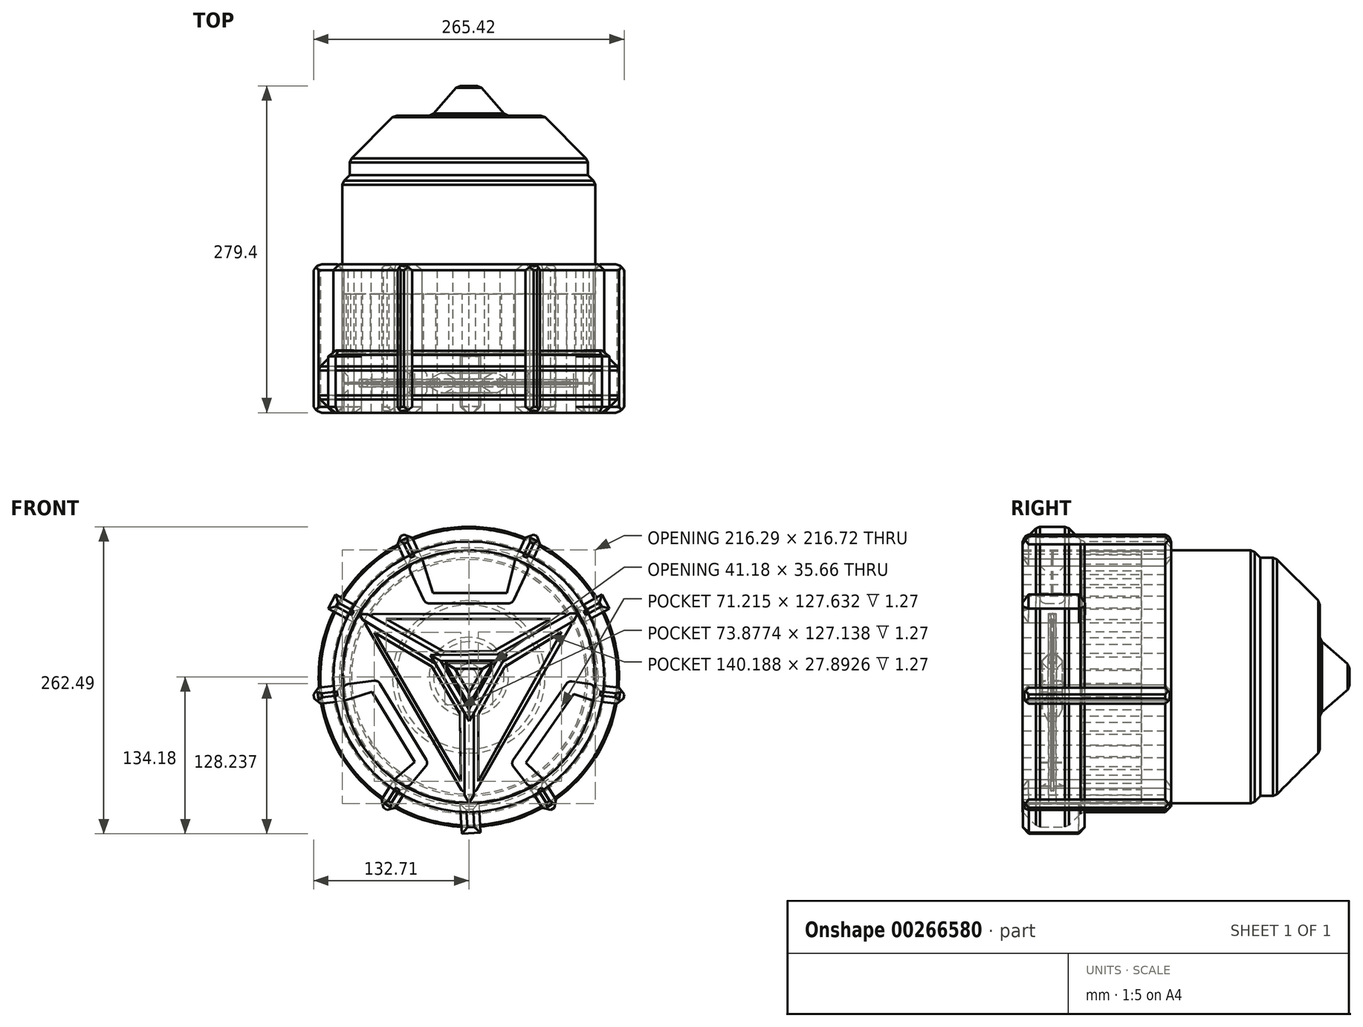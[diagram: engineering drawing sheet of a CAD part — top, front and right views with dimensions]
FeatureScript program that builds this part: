
annotation { "Feature Type Name" : "Feature", "Feature Type Description" : "" }
export const myFeature = defineFeature(function(context is Context, id is Id, definition is map)
    precondition{}
    {
        {
            var Q0;
            Q0=qCreatedBy(makeId("Front.planeOp"),FACE);
            var sketch = newSketch(context, id + "F0", { "sketchPlane" : qUnion([Q0])});
            skLineSegment(sketch, "E0.0", {"start": v(93.23, 54.18) * mm, "end": v(0.3, -107.83) * mm});
            skLineSegment(sketch, "E0.1", {"start": v(0.3, -107.83) * mm, "end": v(-93.54, 53.65) * mm});
            skLineSegment(sketch, "E0.2", {"start": v(-93.54, 53.65) * mm, "end": v(93.23, 54.18) * mm});
            skLineSegment(sketch, "E1.0", {"start": v(-32.94, 18.6) * mm, "end": v(32.57, 19.23) * mm});
            skLineSegment(sketch, "E1.1", {"start": v(32.57, 19.23) * mm, "end": v(0.36, -37.82) * mm});
            skLineSegment(sketch, "E1.2", {"start": v(0.36, -37.82) * mm, "end": v(-32.94, 18.6) * mm});
            skLineSegment(sketch, "E2", {"start": v(4.24, -30.96) * mm, "end": v(4.24, -100.97) * mm});
            skLineSegment(sketch, "E3", {"start": v(-3.69, -100.97) * mm, "end": v(-3.69, -30.96) * mm});
            skLineSegment(sketch, "E4", {"start": v(-86.27, 41.16) * mm, "end": v(-83.71, 36.75) * mm});
            skLineSegment(sketch, "E5", {"start": v(-86.58, 53.67) * mm, "end": v(-24.77, 18.68) * mm});
            skLineSegment(sketch, "E6", {"start": v(-28.9, 11.74) * mm, "end": v(-90.75, 48.87) * mm});
            skLineSegment(sketch, "E7", {"start": v(24.66, 19.15) * mm, "end": v(86.53, 54.16) * mm});
            skLineSegment(sketch, "E8", {"start": v(29.05, 12.98) * mm, "end": v(89.61, 47.87) * mm});
            skCircle(sketch, "E9.cCircle", {"center": v(0, 0) * mm, "radius": 108.36 * mm, "construction": true});
            skLineSegment(sketch, "E9.0", {"start": v(-13.58, -107.5) * mm, "end": v(0, -108.36) * mm});
            skLineSegment(sketch, "E9.1", {"start": v(-26.95, -104.96) * mm, "end": v(-13.58, -107.5) * mm});
            skLineSegment(sketch, "E9.2", {"start": v(-39.9, -100.75) * mm, "end": v(-26.95, -104.96) * mm});
            skLineSegment(sketch, "E9.3", {"start": v(-52.2, -94.96) * mm, "end": v(-39.9, -100.75) * mm});
            skLineSegment(sketch, "E9.4", {"start": v(-63.7, -87.67) * mm, "end": v(-52.2, -94.96) * mm});
            skLineSegment(sketch, "E9.5", {"start": v(-74.18, -79) * mm, "end": v(-63.7, -87.67) * mm});
            skLineSegment(sketch, "E9.6", {"start": v(-83.5, -69.07) * mm, "end": v(-74.18, -79) * mm});
            skLineSegment(sketch, "E9.7", {"start": v(-91.5, -58.06) * mm, "end": v(-83.5, -69.07) * mm});
            skLineSegment(sketch, "E9.8", {"start": v(-98.05, -46.14) * mm, "end": v(-91.5, -58.06) * mm});
            skLineSegment(sketch, "E9.9", {"start": v(-103.06, -33.49) * mm, "end": v(-98.05, -46.14) * mm});
            skLineSegment(sketch, "E9.10", {"start": v(-106.44, -20.3) * mm, "end": v(-103.06, -33.49) * mm});
            skLineSegment(sketch, "E9.11", {"start": v(-108.15, -6.8) * mm, "end": v(-106.44, -20.3) * mm});
            skLineSegment(sketch, "E9.12", {"start": v(-108.15, 6.8) * mm, "end": v(-108.15, -6.8) * mm});
            skLineSegment(sketch, "E9.13", {"start": v(-106.44, 20.3) * mm, "end": v(-108.15, 6.8) * mm});
            skLineSegment(sketch, "E9.14", {"start": v(-103.06, 33.49) * mm, "end": v(-106.44, 20.3) * mm});
            skLineSegment(sketch, "E9.15", {"start": v(-98.05, 46.14) * mm, "end": v(-103.06, 33.49) * mm});
            skLineSegment(sketch, "E9.16", {"start": v(-91.5, 58.06) * mm, "end": v(-98.05, 46.14) * mm});
            skLineSegment(sketch, "E9.17", {"start": v(-83.5, 69.07) * mm, "end": v(-91.5, 58.06) * mm});
            skLineSegment(sketch, "E9.18", {"start": v(-74.18, 79) * mm, "end": v(-83.5, 69.07) * mm});
            skLineSegment(sketch, "E9.19", {"start": v(-63.7, 87.67) * mm, "end": v(-74.18, 79) * mm});
            skLineSegment(sketch, "E9.20", {"start": v(-52.2, 94.96) * mm, "end": v(-63.7, 87.67) * mm});
            skLineSegment(sketch, "E9.21", {"start": v(-39.9, 100.75) * mm, "end": v(-52.2, 94.96) * mm});
            skLineSegment(sketch, "E9.22", {"start": v(-26.95, 104.96) * mm, "end": v(-39.9, 100.75) * mm});
            skLineSegment(sketch, "E9.23", {"start": v(-13.58, 107.5) * mm, "end": v(-26.95, 104.96) * mm});
            skLineSegment(sketch, "E9.24", {"start": v(0, 108.36) * mm, "end": v(-13.58, 107.5) * mm});
            skLineSegment(sketch, "E9.25", {"start": v(13.58, 107.5) * mm, "end": v(0, 108.36) * mm});
            skLineSegment(sketch, "E9.26", {"start": v(26.95, 104.96) * mm, "end": v(13.58, 107.5) * mm});
            skLineSegment(sketch, "E9.27", {"start": v(39.9, 100.75) * mm, "end": v(26.95, 104.96) * mm});
            skLineSegment(sketch, "E9.28", {"start": v(52.2, 94.96) * mm, "end": v(39.9, 100.75) * mm});
            skLineSegment(sketch, "E9.29", {"start": v(63.7, 87.67) * mm, "end": v(52.2, 94.96) * mm});
            skLineSegment(sketch, "E9.30", {"start": v(74.18, 79) * mm, "end": v(63.7, 87.67) * mm});
            skLineSegment(sketch, "E9.31", {"start": v(83.5, 69.07) * mm, "end": v(74.18, 79) * mm});
            skLineSegment(sketch, "E9.32", {"start": v(91.5, 58.06) * mm, "end": v(83.5, 69.07) * mm});
            skLineSegment(sketch, "E9.33", {"start": v(98.05, 46.14) * mm, "end": v(91.5, 58.06) * mm});
            skLineSegment(sketch, "E9.34", {"start": v(103.06, 33.49) * mm, "end": v(98.05, 46.14) * mm});
            skLineSegment(sketch, "E9.35", {"start": v(106.44, 20.3) * mm, "end": v(103.06, 33.49) * mm});
            skLineSegment(sketch, "E9.36", {"start": v(108.15, 6.8) * mm, "end": v(106.44, 20.3) * mm});
            skLineSegment(sketch, "E9.37", {"start": v(108.15, -6.8) * mm, "end": v(108.15, 6.8) * mm});
            skLineSegment(sketch, "E9.38", {"start": v(106.44, -20.3) * mm, "end": v(108.15, -6.8) * mm});
            skLineSegment(sketch, "E9.39", {"start": v(103.06, -33.49) * mm, "end": v(106.44, -20.3) * mm});
            skLineSegment(sketch, "E9.40", {"start": v(98.05, -46.14) * mm, "end": v(103.06, -33.49) * mm});
            skLineSegment(sketch, "E9.41", {"start": v(91.5, -58.06) * mm, "end": v(98.05, -46.14) * mm});
            skLineSegment(sketch, "E9.42", {"start": v(83.5, -69.07) * mm, "end": v(91.5, -58.06) * mm});
            skLineSegment(sketch, "E9.43", {"start": v(74.18, -79) * mm, "end": v(83.5, -69.07) * mm});
            skLineSegment(sketch, "E9.44", {"start": v(63.7, -87.67) * mm, "end": v(74.18, -79) * mm});
            skLineSegment(sketch, "E9.45", {"start": v(52.2, -94.96) * mm, "end": v(63.7, -87.67) * mm});
            skLineSegment(sketch, "E9.46", {"start": v(39.9, -100.75) * mm, "end": v(52.2, -94.96) * mm});
            skLineSegment(sketch, "E9.47", {"start": v(26.95, -104.96) * mm, "end": v(39.9, -100.75) * mm});
            skLineSegment(sketch, "E9.48", {"start": v(13.58, -107.5) * mm, "end": v(26.95, -104.96) * mm});
            skLineSegment(sketch, "E9.49", {"start": v(0, -108.36) * mm, "end": v(13.58, -107.5) * mm});
            skLineSegment(sketch, "E10.0", {"start": v(0, -13.61) * mm, "end": v(-11.79, 6.8) * mm});
            skLineSegment(sketch, "E10.1", {"start": v(-11.79, 6.8) * mm, "end": v(11.79, 6.8) * mm});
            skLineSegment(sketch, "E10.2", {"start": v(11.79, 6.8) * mm, "end": v(0, -13.61) * mm});
            skLineSegment(sketch, "E11", {"start": v(89.74, -14.56) * mm, "end": v(48.6, -73.49) * mm});
            skLineSegment(sketch, "E12", {"start": v(85.15, -3.4) * mm, "end": v(35.89, -73.94) * mm});
            skLineSegment(sketch, "E13", {"start": v(-77.64, -2.95) * mm, "end": v(-34.5, -73.94) * mm});
            skLineSegment(sketch, "E14", {"start": v(-82.82, -12.87) * mm, "end": v(-46.16, -72.86) * mm});
            skLineSegment(sketch, "E15", {"start": v(-37.12, 62.9) * mm, "end": v(37.12, 62.9) * mm});
            skLineSegment(sketch, "E16", {"start": v(-30.7, 71.54) * mm, "end": v(32.57, 71.54) * mm});
            skLineSegment(sketch, "E17", {"start": v(35.89, -73.94) * mm, "end": v(52.2, -94.96) * mm});
            skLineSegment(sketch, "E18", {"start": v(48.6, -73.49) * mm, "end": v(63.7, -87.67) * mm});
            skLineSegment(sketch, "E19", {"start": v(85.15, -3.4) * mm, "end": v(108.15, -6.8) * mm});
            skLineSegment(sketch, "E20", {"start": v(89.74, -14.56) * mm, "end": v(106.44, -20.3) * mm});
            skLineSegment(sketch, "E21", {"start": v(-82.82, -12.87) * mm, "end": v(-106.44, -20.3) * mm});
            skLineSegment(sketch, "E22", {"start": v(-77.64, -2.95) * mm, "end": v(-108.15, -6.8) * mm});
            skLineSegment(sketch, "E23", {"start": v(-46.16, -72.86) * mm, "end": v(-63.7, -87.67) * mm});
            skLineSegment(sketch, "E24", {"start": v(-34.5, -73.94) * mm, "end": v(-52.2, -94.96) * mm});
            skLineSegment(sketch, "E25", {"start": v(-30.7, 71.54) * mm, "end": v(-39.9, 100.75) * mm});
            skLineSegment(sketch, "E26", {"start": v(32.57, 71.54) * mm, "end": v(39.9, 100.75) * mm});
            skLineSegment(sketch, "E27", {"start": v(37.12, 62.9) * mm, "end": v(52.2, 94.96) * mm});
            skLineSegment(sketch, "E28", {"start": v(-37.12, 62.9) * mm, "end": v(-52.2, 94.96) * mm});
            skCircle(sketch, "E29.0", {"center": v(0, 0) * mm, "radius": 128.3 * mm});
            skSolve(sketch);
        }
        {
            var Q0;
            Q0=makeQuery(id+"F0.imprint","IMPRINT",FACE,{"disambiguationData":[TD([[makeQuery(id+"F0.imprint","IMPRINT",EDGE,{"derivedFrom":sQuery(id+"F0.wireOp",EDGE,"E9.0")}),-1.0]])]});
            extrude(context, id + "F1", {"entities" : qUnion([Q0]), "endBound" : BoundingType.SYMMETRIC, "depth" : 50.8 * mm});
        }
        {
            var Q0;
            {var subQ0=sQuery(id+"F0.wireOp",EDGE,"E5");Q0=makeQuery(id+"F0.imprint","IMPRINT",FACE,{"disambiguationData":[TD([[makeQuery(id+"F0.imprint","IMPRINT",EDGE,{"derivedFrom":subQ0}),1.0]])]});}
            var Q1;
            {var subQ0=sQuery(id+"F0.wireOp",EDGE,"E3");Q1=makeQuery(id+"F0.imprint","IMPRINT",FACE,{"disambiguationData":[TD([[makeQuery(id+"F0.imprint","IMPRINT",EDGE,{"derivedFrom":subQ0}),1.0]])]});}
            var Q2;
            {var subQ0=sQuery(id+"F0.wireOp",EDGE,"E2");Q2=makeQuery(id+"F0.imprint","IMPRINT",FACE,{"disambiguationData":[TD([[makeQuery(id+"F0.imprint","IMPRINT",EDGE,{"derivedFrom":subQ0}),1.0]])]});}
            extrude(context, id + "F2", {"entities" : qUnion([Q0, Q1, Q2]), "endBound" : BoundingType.SYMMETRIC, "depth" : 2.54 * mm});
        }
        {
            var Q0;
            {var subQ7=sQuery(id+"F0.wireOp",EDGE,"E5");Q0=makeQuery(id+"F0.imprint","IMPRINT",FACE,{"disambiguationData":[TD([[makeQuery(id+"F0.imprint","IMPRINT",EDGE,{"derivedFrom":subQ7}),-1.0]])]});}
            var Q1;
            {var subQ4=sQuery(id+"F0.wireOp",EDGE,"E7");Q1=makeQuery(id+"F0.imprint","IMPRINT",FACE,{"disambiguationData":[TD([[makeQuery(id+"F0.imprint","IMPRINT",EDGE,{"derivedFrom":subQ4}),-1.0]])]});}
            var Q2;
            {var subQ3=sQuery(id+"F0.wireOp",EDGE,"E2");Q2=makeQuery(id+"F0.imprint","IMPRINT",FACE,{"disambiguationData":[TD([[makeQuery(id+"F0.imprint","IMPRINT",EDGE,{"derivedFrom":subQ3}),-1.0]])]});}
            extrude(context, id + "F3", {"entities" : qUnion([Q0, Q1, Q2]), "endBound" : BoundingType.SYMMETRIC, "depth" : 6.35 * mm});
        }
        {
            var Q0;
            Q0=makeQuery(id+"F0.imprint","IMPRINT",FACE,{"disambiguationData":[TD([[makeQuery(id+"F0.imprint","IMPRINT",EDGE,{"derivedFrom":sQuery(id+"F0.wireOp",EDGE,"E10.0")}),-1.0]])]});
            var Q1;
            {var subQ0=sQuery(id+"F0.wireOp",EDGE,"E4");Q1=makeQuery(id+"F0.imprint","IMPRINT",FACE,{"disambiguationData":[TD([[makeQuery(id+"F0.imprint","IMPRINT",EDGE,{"derivedFrom":subQ0}),-1.0]])]});}
            var Q2;
            Q2=makeQuery(id+"F0.imprint","IMPRINT",FACE,{"disambiguationData":[TD([[makeQuery(id+"F0.imprint","IMPRINT",EDGE,{"derivedFrom":sQuery(id+"F0.wireOp",EDGE,"E9.22")}),1.0]])]});
            var Q3;
            Q3=makeQuery(id+"F0.imprint","IMPRINT",FACE,{"disambiguationData":[TD([[makeQuery(id+"F0.imprint","IMPRINT",EDGE,{"derivedFrom":sQuery(id+"F0.wireOp",EDGE,"E9.39")}),1.0]])]});
            var Q4;
            Q4=makeQuery(id+"F0.imprint","IMPRINT",FACE,{"disambiguationData":[TD([[makeQuery(id+"F0.imprint","IMPRINT",EDGE,{"derivedFrom":sQuery(id+"F0.wireOp",EDGE,"E9.5")}),1.0]])]});
            extrude(context, id + "F4", {"entities" : qUnion([Q0, Q1, Q2, Q3, Q4]), "endBound" : BoundingType.SYMMETRIC, "depth" : 1.27 * mm});
        }
        {
            var Q0;
            Q0=makeQuery(id+"F0.imprint","IMPRINT",FACE,{"disambiguationData":[TD([[makeQuery(id+"F0.imprint","IMPRINT",EDGE,{"derivedFrom":sQuery(id+"F0.wireOp",EDGE,"E9.21")}),1.0]])]});
            var Q1;
            Q1=makeQuery(id+"F0.imprint","IMPRINT",FACE,{"disambiguationData":[TD([[makeQuery(id+"F0.imprint","IMPRINT",EDGE,{"derivedFrom":sQuery(id+"F0.wireOp",EDGE,"E9.4")}),1.0]])]});
            var Q2;
            Q2=makeQuery(id+"F0.imprint","IMPRINT",FACE,{"disambiguationData":[TD([[makeQuery(id+"F0.imprint","IMPRINT",EDGE,{"derivedFrom":sQuery(id+"F0.wireOp",EDGE,"E9.38")}),1.0]])]});
            extrude(context, id + "F5", {"entities" : qUnion([Q0, Q1, Q2]), "endBound" : BoundingType.SYMMETRIC, "depth" : 21.59 * mm});
        }
        {
            var Q0;
            Q0=makeQuery(id+"F0.imprint","IMPRINT",FACE,{"disambiguationData":[TD([[makeQuery(id+"F0.imprint","IMPRINT",EDGE,{"derivedFrom":sQuery(id+"F0.wireOp",EDGE,"E10.0")}),1.0]])]});
            extrude(context, id + "F6", {"entities" : qUnion([Q0]), "endBound" : BoundingType.SYMMETRIC, "depth" : 17.02 * mm});
        }
        {
            var Q0;
            Q0=makeQuery(id+"F1.opExtrude","CAP_EDGE",EDGE,{"disambiguationData":[OSD([sQuery(id+"F0.wireOp",EDGE,"E29.0")])],"isStart":false});
            var Q1;
            Q1=makeQuery(id+"F1.opExtrude","CAP_EDGE",EDGE,{"disambiguationData":[OSD([sQuery(id+"F0.wireOp",EDGE,"E29.0")])],"isStart":true});
            chamfer(context, id + "F7", {"entities" : qUnion([Q0, Q1]), "width" : 12.7 * mm, "tangentPropagation" : true});
        }
        {
            var Q0;
            Q0=makeQuery(id+"F5.opExtrude","SWEPT_FACE",FACE,{"disambiguationData":[OSD([sQuery(id+"F0.wireOp",EDGE,"E15")])]});
            var Q1;
            Q1=makeQuery(id+"F5.opExtrude","SWEPT_FACE",FACE,{"disambiguationData":[OSD([sQuery(id+"F0.wireOp",EDGE,"E28")])]});
            var Q2;
            Q2=makeQuery(id+"F5.opExtrude","SWEPT_FACE",FACE,{"disambiguationData":[OSD([sQuery(id+"F0.wireOp",EDGE,"E27")])]});
            var Q3;
            Q3=makeQuery(id+"F5.opExtrude","SWEPT_FACE",FACE,{"disambiguationData":[OSD([sQuery(id+"F0.wireOp",EDGE,"E13")])]});
            var Q4;
            Q4=makeQuery(id+"F5.opExtrude","SWEPT_FACE",FACE,{"disambiguationData":[OSD([sQuery(id+"F0.wireOp",EDGE,"E24")])]});
            var Q5;
            Q5=makeQuery(id+"F5.opExtrude","SWEPT_FACE",FACE,{"disambiguationData":[OSD([sQuery(id+"F0.wireOp",EDGE,"E22")])]});
            var Q6;
            Q6=makeQuery(id+"F5.opExtrude","SWEPT_FACE",FACE,{"disambiguationData":[OSD([sQuery(id+"F0.wireOp",EDGE,"E12")])]});
            var Q7;
            Q7=makeQuery(id+"F5.opExtrude","SWEPT_FACE",FACE,{"disambiguationData":[OSD([sQuery(id+"F0.wireOp",EDGE,"E19")])]});
            var Q8;
            Q8=makeQuery(id+"F5.opExtrude","SWEPT_FACE",FACE,{"disambiguationData":[OSD([sQuery(id+"F0.wireOp",EDGE,"E17")])]});
            fillet(context, id + "F8", {"entities" : qUnion([Q0, Q1, Q2, Q3, Q4, Q5, Q6, Q7, Q8]), "radius" : 5.08 * mm, "tangentPropagation" : true, "allowEdgeOverflow" : false});
        }
        {
            var Q0;
            Q0=makeQuery(id+"F2.opExtrude","SWEPT_FACE",FACE,{"disambiguationData":[OSD([sQuery(id+"F0.wireOp",EDGE,"E0.0")])]});
            var Q1;
            Q1=makeQuery(id+"F2.opExtrude","SWEPT_FACE",FACE,{"disambiguationData":[OSD([sQuery(id+"F0.wireOp",EDGE,"E0.2")])]});
            var Q2;
            Q2=makeQuery(id+"F2.opExtrude","SWEPT_FACE",FACE,{"disambiguationData":[OSD([sQuery(id+"F0.wireOp",EDGE,"E0.1"),sQuery(id+"F0.wireOp",EDGE,"E4")])]});
            fillet(context, id + "F9", {"entities" : qUnion([Q0, Q1, Q2]), "radius" : 1.27 * mm, "tangentPropagation" : true, "allowEdgeOverflow" : false});
        }
        {
            var Q0;
            Q0=makeQuery(id+"F6.opExtrude","CAP_FACE",FACE,{"disambiguationData":[OSD([sQuery(id+"F0.wireOp",EDGE,"E1.0"),sQuery(id+"F0.wireOp",EDGE,"E1.1"),sQuery(id+"F0.wireOp",EDGE,"E1.2"),sQuery(id+"F0.wireOp",EDGE,"E10.0"),sQuery(id+"F0.wireOp",EDGE,"E10.1"),sQuery(id+"F0.wireOp",EDGE,"E10.2")])],"isStart":false});
            var Q1;
            Q1=makeQuery(id+"F6.opExtrude","CAP_FACE",FACE,{"disambiguationData":[OSD([sQuery(id+"F0.wireOp",EDGE,"E1.0"),sQuery(id+"F0.wireOp",EDGE,"E1.1"),sQuery(id+"F0.wireOp",EDGE,"E1.2"),sQuery(id+"F0.wireOp",EDGE,"E10.0"),sQuery(id+"F0.wireOp",EDGE,"E10.1"),sQuery(id+"F0.wireOp",EDGE,"E10.2")])],"isStart":true});
            chamfer(context, id + "F10", {"entities" : qUnion([Q0, Q1]), "width" : 5.08 * mm, "tangentPropagation" : true});
        }
        {
            var Q0;
            Q0=makeQuery(id+"F1.opExtrude","CAP_FACE",FACE,{"disambiguationData":[OSD([sQuery(id+"F0.wireOp",EDGE,"E9.0"),sQuery(id+"F0.wireOp",EDGE,"E9.1"),sQuery(id+"F0.wireOp",EDGE,"E9.2"),sQuery(id+"F0.wireOp",EDGE,"E9.3"),sQuery(id+"F0.wireOp",EDGE,"E9.4"),sQuery(id+"F0.wireOp",EDGE,"E9.5"),sQuery(id+"F0.wireOp",EDGE,"E9.6"),sQuery(id+"F0.wireOp",EDGE,"E9.7"),sQuery(id+"F0.wireOp",EDGE,"E9.8"),sQuery(id+"F0.wireOp",EDGE,"E9.9"),sQuery(id+"F0.wireOp",EDGE,"E9.10"),sQuery(id+"F0.wireOp",EDGE,"E9.11"),sQuery(id+"F0.wireOp",EDGE,"E9.12"),sQuery(id+"F0.wireOp",EDGE,"E9.13"),sQuery(id+"F0.wireOp",EDGE,"E9.14"),sQuery(id+"F0.wireOp",EDGE,"E9.15"),sQuery(id+"F0.wireOp",EDGE,"E9.16"),sQuery(id+"F0.wireOp",EDGE,"E9.17"),sQuery(id+"F0.wireOp",EDGE,"E9.18"),sQuery(id+"F0.wireOp",EDGE,"E9.19"),sQuery(id+"F0.wireOp",EDGE,"E9.20"),sQuery(id+"F0.wireOp",EDGE,"E9.21"),sQuery(id+"F0.wireOp",EDGE,"E9.22"),sQuery(id+"F0.wireOp",EDGE,"E9.23"),sQuery(id+"F0.wireOp",EDGE,"E9.24"),sQuery(id+"F0.wireOp",EDGE,"E9.25"),sQuery(id+"F0.wireOp",EDGE,"E9.26"),sQuery(id+"F0.wireOp",EDGE,"E9.27"),sQuery(id+"F0.wireOp",EDGE,"E9.28"),sQuery(id+"F0.wireOp",EDGE,"E9.29"),sQuery(id+"F0.wireOp",EDGE,"E9.30"),sQuery(id+"F0.wireOp",EDGE,"E9.31"),sQuery(id+"F0.wireOp",EDGE,"E9.32"),sQuery(id+"F0.wireOp",EDGE,"E9.33"),sQuery(id+"F0.wireOp",EDGE,"E9.34"),sQuery(id+"F0.wireOp",EDGE,"E9.35"),sQuery(id+"F0.wireOp",EDGE,"E9.36"),sQuery(id+"F0.wireOp",EDGE,"E9.37"),sQuery(id+"F0.wireOp",EDGE,"E9.38"),sQuery(id+"F0.wireOp",EDGE,"E9.39"),sQuery(id+"F0.wireOp",EDGE,"E9.40"),sQuery(id+"F0.wireOp",EDGE,"E9.41"),sQuery(id+"F0.wireOp",EDGE,"E9.42"),sQuery(id+"F0.wireOp",EDGE,"E9.43"),sQuery(id+"F0.wireOp",EDGE,"E9.44"),sQuery(id+"F0.wireOp",EDGE,"E9.45"),sQuery(id+"F0.wireOp",EDGE,"E9.46"),sQuery(id+"F0.wireOp",EDGE,"E9.47"),sQuery(id+"F0.wireOp",EDGE,"E9.48"),sQuery(id+"F0.wireOp",EDGE,"E9.49"),sQuery(id+"F0.wireOp",EDGE,"E29.0")])],"isStart":true});
            extrude(context, id + "F11", {"entities" : qUnion([Q0]), "operationType" : NewBodyOperationType.ADD, "depth" : 76.2 * mm});
        }
        {
            var Q0;
            Q0=makeQuery(id+"F11.opExtrude","CAP_FACE",FACE,{"disambiguationData":[OSD([sQuery(id+"F0.wireOp",EDGE,"E9.0"),sQuery(id+"F0.wireOp",EDGE,"E9.1"),sQuery(id+"F0.wireOp",EDGE,"E9.2"),sQuery(id+"F0.wireOp",EDGE,"E9.3"),sQuery(id+"F0.wireOp",EDGE,"E9.4"),sQuery(id+"F0.wireOp",EDGE,"E9.5"),sQuery(id+"F0.wireOp",EDGE,"E9.6"),sQuery(id+"F0.wireOp",EDGE,"E9.7"),sQuery(id+"F0.wireOp",EDGE,"E9.8"),sQuery(id+"F0.wireOp",EDGE,"E9.9"),sQuery(id+"F0.wireOp",EDGE,"E9.10"),sQuery(id+"F0.wireOp",EDGE,"E9.11"),sQuery(id+"F0.wireOp",EDGE,"E9.12"),sQuery(id+"F0.wireOp",EDGE,"E9.13"),sQuery(id+"F0.wireOp",EDGE,"E9.14"),sQuery(id+"F0.wireOp",EDGE,"E9.15"),sQuery(id+"F0.wireOp",EDGE,"E9.16"),sQuery(id+"F0.wireOp",EDGE,"E9.17"),sQuery(id+"F0.wireOp",EDGE,"E9.18"),sQuery(id+"F0.wireOp",EDGE,"E9.19"),sQuery(id+"F0.wireOp",EDGE,"E9.20"),sQuery(id+"F0.wireOp",EDGE,"E9.21"),sQuery(id+"F0.wireOp",EDGE,"E9.22"),sQuery(id+"F0.wireOp",EDGE,"E9.23"),sQuery(id+"F0.wireOp",EDGE,"E9.24"),sQuery(id+"F0.wireOp",EDGE,"E9.25"),sQuery(id+"F0.wireOp",EDGE,"E9.26"),sQuery(id+"F0.wireOp",EDGE,"E9.27"),sQuery(id+"F0.wireOp",EDGE,"E9.28"),sQuery(id+"F0.wireOp",EDGE,"E9.29"),sQuery(id+"F0.wireOp",EDGE,"E9.30"),sQuery(id+"F0.wireOp",EDGE,"E9.31"),sQuery(id+"F0.wireOp",EDGE,"E9.32"),sQuery(id+"F0.wireOp",EDGE,"E9.33"),sQuery(id+"F0.wireOp",EDGE,"E9.34"),sQuery(id+"F0.wireOp",EDGE,"E9.35"),sQuery(id+"F0.wireOp",EDGE,"E9.36"),sQuery(id+"F0.wireOp",EDGE,"E9.37"),sQuery(id+"F0.wireOp",EDGE,"E9.38"),sQuery(id+"F0.wireOp",EDGE,"E9.39"),sQuery(id+"F0.wireOp",EDGE,"E9.40"),sQuery(id+"F0.wireOp",EDGE,"E9.41"),sQuery(id+"F0.wireOp",EDGE,"E9.42"),sQuery(id+"F0.wireOp",EDGE,"E9.43"),sQuery(id+"F0.wireOp",EDGE,"E9.44"),sQuery(id+"F0.wireOp",EDGE,"E9.45"),sQuery(id+"F0.wireOp",EDGE,"E9.46"),sQuery(id+"F0.wireOp",EDGE,"E9.47"),sQuery(id+"F0.wireOp",EDGE,"E9.48"),sQuery(id+"F0.wireOp",EDGE,"E9.49"),sQuery(id+"F0.wireOp",EDGE,"E29.0")])],"isStart":false});
            var sketch = newSketch(context, id + "F12", { "sketchPlane" : qUnion([Q0])});
            skCircle(sketch, "E30", {"center": v(0, 0) * mm, "radius": 108.15 * mm});
            skSolve(sketch);
        }
        {
            var Q0;
            Q0=qSketchRegion(id+"F12",true);
            extrude(context, id + "F13", {"entities" : qUnion([Q0]), "depth" : 50.8 * mm});
        }
        {
            var Q0;
            Q0=makeQuery(id+"F11.opExtrude","SWEPT_FACE",FACE,{"disambiguationData":[OSD([sQuery(id+"F0.wireOp",EDGE,"E9.0"),sQuery(id+"F0.wireOp",EDGE,"E9.1"),sQuery(id+"F0.wireOp",EDGE,"E9.2"),sQuery(id+"F0.wireOp",EDGE,"E9.3"),sQuery(id+"F0.wireOp",EDGE,"E9.4"),sQuery(id+"F0.wireOp",EDGE,"E9.5"),sQuery(id+"F0.wireOp",EDGE,"E9.6"),sQuery(id+"F0.wireOp",EDGE,"E9.7"),sQuery(id+"F0.wireOp",EDGE,"E9.8"),sQuery(id+"F0.wireOp",EDGE,"E9.9"),sQuery(id+"F0.wireOp",EDGE,"E9.10"),sQuery(id+"F0.wireOp",EDGE,"E9.11"),sQuery(id+"F0.wireOp",EDGE,"E9.12"),sQuery(id+"F0.wireOp",EDGE,"E9.13"),sQuery(id+"F0.wireOp",EDGE,"E9.14"),sQuery(id+"F0.wireOp",EDGE,"E9.15"),sQuery(id+"F0.wireOp",EDGE,"E9.16"),sQuery(id+"F0.wireOp",EDGE,"E9.17"),sQuery(id+"F0.wireOp",EDGE,"E9.18"),sQuery(id+"F0.wireOp",EDGE,"E9.19"),sQuery(id+"F0.wireOp",EDGE,"E9.20"),sQuery(id+"F0.wireOp",EDGE,"E9.21"),sQuery(id+"F0.wireOp",EDGE,"E9.22"),sQuery(id+"F0.wireOp",EDGE,"E9.23"),sQuery(id+"F0.wireOp",EDGE,"E9.24"),sQuery(id+"F0.wireOp",EDGE,"E9.25"),sQuery(id+"F0.wireOp",EDGE,"E9.26"),sQuery(id+"F0.wireOp",EDGE,"E9.27"),sQuery(id+"F0.wireOp",EDGE,"E9.28"),sQuery(id+"F0.wireOp",EDGE,"E9.29"),sQuery(id+"F0.wireOp",EDGE,"E9.30"),sQuery(id+"F0.wireOp",EDGE,"E9.31"),sQuery(id+"F0.wireOp",EDGE,"E9.32"),sQuery(id+"F0.wireOp",EDGE,"E9.33"),sQuery(id+"F0.wireOp",EDGE,"E9.34"),sQuery(id+"F0.wireOp",EDGE,"E9.35"),sQuery(id+"F0.wireOp",EDGE,"E9.36"),sQuery(id+"F0.wireOp",EDGE,"E9.37"),sQuery(id+"F0.wireOp",EDGE,"E9.38"),sQuery(id+"F0.wireOp",EDGE,"E9.39"),sQuery(id+"F0.wireOp",EDGE,"E9.40"),sQuery(id+"F0.wireOp",EDGE,"E9.41"),sQuery(id+"F0.wireOp",EDGE,"E9.42"),sQuery(id+"F0.wireOp",EDGE,"E9.43"),sQuery(id+"F0.wireOp",EDGE,"E9.44"),sQuery(id+"F0.wireOp",EDGE,"E9.45"),sQuery(id+"F0.wireOp",EDGE,"E9.46"),sQuery(id+"F0.wireOp",EDGE,"E9.47"),sQuery(id+"F0.wireOp",EDGE,"E9.48"),sQuery(id+"F0.wireOp",EDGE,"E9.49"),sQuery(id+"F0.wireOp",EDGE,"E29.0")])]});
            chamfer(context, id + "F14", {"entities" : qUnion([Q0]), "width" : 5.08 * mm, "tangentPropagation" : true});
        }
        {
            var Q0;
            Q0=makeQuery(id+"F13.opExtrude","CAP_FACE",FACE,{"disambiguationData":[OSD([sQuery(id+"F12.wireOp",EDGE,"E30")])],"isStart":false});
            extrude(context, id + "F15", {"entities" : qUnion([Q0]), "operationType" : NewBodyOperationType.ADD, "oppositeDirection" : true, "depth" : 76.2 * mm});
        }
        {
            var Q0;
            Q0=makeQuery(id+"F13.opExtrude","CAP_FACE",FACE,{"disambiguationData":[OSD([sQuery(id+"F12.wireOp",EDGE,"E30")])],"isStart":false});
            extrude(context, id + "F16", {"entities" : qUnion([Q0]), "operationType" : NewBodyOperationType.ADD, "depth" : 25.4 * mm});
        }
        {
            var Q0;
            Q0=makeQuery(id+"F16.opExtrude","CAP_FACE",FACE,{"disambiguationData":[OSD([sQuery(id+"F12.wireOp",EDGE,"E30")])],"isStart":false});
            chamfer(context, id + "F17", {"entities" : qUnion([Q0]), "width" : 6.35 * mm, "tangentPropagation" : true});
        }
        {
            var Q0;
            Q0=makeQuery(id+"F16.opExtrude","CAP_FACE",FACE,{"disambiguationData":[OSD([sQuery(id+"F12.wireOp",EDGE,"E30")])],"isStart":false});
            extrude(context, id + "F18", {"entities" : qUnion([Q0]), "operationType" : NewBodyOperationType.ADD, "depth" : 50.8 * mm});
        }
        {
            var Q0;
            Q0=makeQuery(id+"F18.opExtrude","CAP_FACE",FACE,{"disambiguationData":[OSD([sQuery(id+"F12.wireOp",EDGE,"E30")])],"isStart":false});
            chamfer(context, id + "F19", {"entities" : qUnion([Q0]), "width" : 38.1 * mm, "tangentPropagation" : true});
        }
        {
            var Q0;
            Q0=makeQuery(id+"F18.opExtrude","CAP_FACE",FACE,{"disambiguationData":[OSD([sQuery(id+"F12.wireOp",EDGE,"E30")])],"isStart":false});
            var sketch = newSketch(context, id + "F20", { "sketchPlane" : qUnion([Q0])});
            skCircle(sketch, "E31", {"center": v(0, 0) * mm, "radius": 31.55 * mm});
            skSolve(sketch);
        }
        {
            var Q0;
            Q0=makeQuery(id+"F20.imprint","IMPRINT",FACE,{"disambiguationData":[TD([[makeQuery(id+"F20.imprint","IMPRINT",EDGE,{"derivedFrom":sQuery(id+"F20.wireOp",EDGE,"E31")}),1.0]])]});
            cPlane(context, id + "F21", {"entities" : qUnion([Q0]), "cplaneType" : CPlaneType.OFFSET, "offset" : 25.4 * mm, "width" : 152.4 * mm, "height" : 152.4 * mm});
        }
        {
            var Q0;
            Q0=qCreatedBy(id+"F21.planeOp",FACE);
            var sketch = newSketch(context, id + "F22", { "sketchPlane" : qUnion([Q0])});
            skCircle(sketch, "E32", {"center": v(0, 0) * mm, "radius": 9.52 * mm});
            skSolve(sketch);
        }
        {
            var Q1;
            Q1=makeQuery(id+"F22.imprint","IMPRINT",FACE,{"disambiguationData":[TD([[makeQuery(id+"F22.imprint","IMPRINT",EDGE,{"derivedFrom":sQuery(id+"F22.wireOp",EDGE,"E32")}),1.0]])]});
            var Q2;
            Q2=makeQuery(id+"F20.imprint","IMPRINT",FACE,{"disambiguationData":[TD([[makeQuery(id+"F20.imprint","IMPRINT",EDGE,{"derivedFrom":sQuery(id+"F20.wireOp",EDGE,"E31")}),1.0]])]});
            loft(context, id + "F23", {"operationType" : NewBodyOperationType.ADD, "sheetProfilesArray" : [{ "sheetProfileEntities" : qUnion([Q1]) }, { "sheetProfileEntities" : qUnion([Q2]) }]});
        }
        {
            var Q0;
            Q0=makeQuery(id+"F4.opExtrude","CAP_FACE",FACE,{"disambiguationData":[OSD([sQuery(id+"F0.wireOp",EDGE,"E10.0"),sQuery(id+"F0.wireOp",EDGE,"E10.1"),sQuery(id+"F0.wireOp",EDGE,"E10.2")])],"isStart":true});
            cPlane(context, id + "F24", {"entities" : qUnion([Q0]), "cplaneType" : CPlaneType.OFFSET, "offset" : 12.7 * mm, "width" : 152.4 * mm, "height" : 152.4 * mm});
        }
        {
            var Q0;
            Q0=makeQuery(id+"F4.opExtrude","CAP_FACE",FACE,{"disambiguationData":[OSD([sQuery(id+"F0.wireOp",EDGE,"E10.0"),sQuery(id+"F0.wireOp",EDGE,"E10.1"),sQuery(id+"F0.wireOp",EDGE,"E10.2")])],"isStart":false});
            cPlane(context, id + "F25", {"entities" : qUnion([Q0]), "cplaneType" : CPlaneType.OFFSET, "offset" : 6.35 * mm, "width" : 152.4 * mm, "height" : 152.4 * mm});
        }
        {
            var Q0;
            {var subQ0=sQuery(id+"F0.wireOp",EDGE,"E9.11");Q0=makeQuery(id+"F11.boolean.opBoolean","MERGE",FACE,{"derivedFrom":[makeQuery(id+"F1.opExtrude","SWEPT_FACE",FACE,{"disambiguationData":[OSD([subQ0])]}),makeQuery(id+"F11.opExtrude","SWEPT_FACE",FACE,{"disambiguationData":[OSD([subQ0])]})]});}
            extrude(context, id + "F26", {"entities" : qUnion([Q0]), "oppositeDirection" : true, "depth" : 25.4 * mm});
        }
        {
            var Q0;
            {var subQ0=sQuery(id+"F0.wireOp",EDGE,"E9.4");Q0=makeQuery(id+"F11.boolean.opBoolean","MERGE",FACE,{"derivedFrom":[makeQuery(id+"F1.opExtrude","SWEPT_FACE",FACE,{"disambiguationData":[OSD([subQ0])]}),makeQuery(id+"F11.opExtrude","SWEPT_FACE",FACE,{"disambiguationData":[OSD([subQ0])]})]});}
            extrude(context, id + "F27", {"entities" : qUnion([Q0]), "oppositeDirection" : true, "depth" : 25.4 * mm});
        }
        {
            var Q0;
            {var subQ0=sQuery(id+"F0.wireOp",EDGE,"E9.38");Q0=makeQuery(id+"F11.boolean.opBoolean","MERGE",FACE,{"derivedFrom":[makeQuery(id+"F1.opExtrude","SWEPT_FACE",FACE,{"disambiguationData":[OSD([subQ0])]}),makeQuery(id+"F11.opExtrude","SWEPT_FACE",FACE,{"disambiguationData":[OSD([subQ0])]})]});}
            extrude(context, id + "F28", {"entities" : qUnion([Q0]), "oppositeDirection" : true, "depth" : 25.4 * mm});
        }
        {
            var Q0;
            {var subQ0=sQuery(id+"F0.wireOp",EDGE,"E9.45");Q0=makeQuery(id+"F11.boolean.opBoolean","MERGE",FACE,{"derivedFrom":[makeQuery(id+"F1.opExtrude","SWEPT_FACE",FACE,{"disambiguationData":[OSD([subQ0])]}),makeQuery(id+"F11.opExtrude","SWEPT_FACE",FACE,{"disambiguationData":[OSD([subQ0])]})]});}
            extrude(context, id + "F29", {"entities" : qUnion([Q0]), "oppositeDirection" : true, "depth" : 25.4 * mm});
        }
        {
            var Q0;
            {var subQ0=sQuery(id+"F0.wireOp",EDGE,"E9.28");Q0=makeQuery(id+"F11.boolean.opBoolean","MERGE",FACE,{"derivedFrom":[makeQuery(id+"F1.opExtrude","SWEPT_FACE",FACE,{"disambiguationData":[OSD([subQ0])]}),makeQuery(id+"F11.opExtrude","SWEPT_FACE",FACE,{"disambiguationData":[OSD([subQ0])]})]});}
            extrude(context, id + "F30", {"entities" : qUnion([Q0]), "oppositeDirection" : true, "depth" : 25.4 * mm});
        }
        {
            var Q0;
            {var subQ0=sQuery(id+"F0.wireOp",EDGE,"E9.21");Q0=makeQuery(id+"F11.boolean.opBoolean","MERGE",FACE,{"derivedFrom":[makeQuery(id+"F1.opExtrude","SWEPT_FACE",FACE,{"disambiguationData":[OSD([subQ0])]}),makeQuery(id+"F11.opExtrude","SWEPT_FACE",FACE,{"disambiguationData":[OSD([subQ0])]})]});}
            extrude(context, id + "F31", {"entities" : qUnion([Q0]), "oppositeDirection" : true, "depth" : 25.4 * mm});
        }
        {
            var Q0;
            Q0=makeQuery(id+"F29.opExtrude","CAP_FACE",FACE,{"disambiguationData":[OSD([sQuery(id+"F0.wireOp",EDGE,"E9.45")])],"isStart":false});
            chamfer(context, id + "F32", {"entities" : qUnion([Q0]), "width" : 5.08 * mm, "tangentPropagation" : true});
        }
        {
            var Q0;
            Q0=makeQuery(id+"F27.opExtrude","CAP_FACE",FACE,{"disambiguationData":[OSD([sQuery(id+"F0.wireOp",EDGE,"E9.4")])],"isStart":false});
            chamfer(context, id + "F33", {"entities" : qUnion([Q0]), "width" : 5.08 * mm, "tangentPropagation" : true});
        }
        {
            var Q0;
            Q0=makeQuery(id+"F28.opExtrude","CAP_FACE",FACE,{"disambiguationData":[OSD([sQuery(id+"F0.wireOp",EDGE,"E9.38")])],"isStart":false});
            chamfer(context, id + "F34", {"entities" : qUnion([Q0]), "width" : 5.08 * mm, "tangentPropagation" : true});
        }
        {
            var Q0;
            Q0=makeQuery(id+"F30.opExtrude","CAP_FACE",FACE,{"disambiguationData":[OSD([sQuery(id+"F0.wireOp",EDGE,"E9.28")])],"isStart":false});
            chamfer(context, id + "F35", {"entities" : qUnion([Q0]), "width" : 5.08 * mm, "tangentPropagation" : true});
        }
        {
            var Q0;
            Q0=makeQuery(id+"F31.opExtrude","CAP_FACE",FACE,{"disambiguationData":[OSD([sQuery(id+"F0.wireOp",EDGE,"E9.21")])],"isStart":false});
            chamfer(context, id + "F36", {"entities" : qUnion([Q0]), "width" : 5.08 * mm, "tangentPropagation" : true});
        }
        {
            var Q0;
            Q0=makeQuery(id+"F26.opExtrude","CAP_FACE",FACE,{"disambiguationData":[OSD([sQuery(id+"F0.wireOp",EDGE,"E9.11")])],"isStart":false});
            chamfer(context, id + "F37", {"entities" : qUnion([Q0]), "width" : 5.08 * mm, "tangentPropagation" : true});
        }
        {
            var Q0;
            {var subQ0=sQuery(id+"F0.wireOp",EDGE,"E9.4");Q0=makeQuery(id+"F27.opExtrude","SWEPT_FACE",FACE,{"disambiguationData":[OSD([subQ0]),TDD([makeQuery(id+"F1.opExtrude","CAP_EDGE",EDGE,{"disambiguationData":[OSD([subQ0])],"isStart":false})])]});}
            chamfer(context, id + "F38", {"entities" : qUnion([Q0]), "width" : 5.08 * mm, "tangentPropagation" : true});
        }
        {
            var Q0;
            {var subQ0=sQuery(id+"F0.wireOp",EDGE,"E9.11");Q0=makeQuery(id+"F26.opExtrude","SWEPT_FACE",FACE,{"disambiguationData":[OSD([subQ0]),TDD([makeQuery(id+"F1.opExtrude","CAP_EDGE",EDGE,{"disambiguationData":[OSD([subQ0])],"isStart":false})])]});}
            var Q1;
            {var subQ0=sQuery(id+"F0.wireOp",EDGE,"E9.21");Q1=makeQuery(id+"F31.opExtrude","SWEPT_FACE",FACE,{"disambiguationData":[OSD([subQ0]),TDD([makeQuery(id+"F1.opExtrude","CAP_EDGE",EDGE,{"disambiguationData":[OSD([subQ0])],"isStart":false})])]});}
            var Q2;
            {var subQ0=sQuery(id+"F0.wireOp",EDGE,"E9.28");Q2=makeQuery(id+"F30.opExtrude","SWEPT_FACE",FACE,{"disambiguationData":[OSD([subQ0]),TDD([makeQuery(id+"F1.opExtrude","CAP_EDGE",EDGE,{"disambiguationData":[OSD([subQ0])],"isStart":false})])]});}
            var Q3;
            {var subQ0=sQuery(id+"F0.wireOp",EDGE,"E9.38");Q3=makeQuery(id+"F28.opExtrude","SWEPT_FACE",FACE,{"disambiguationData":[OSD([subQ0]),TDD([makeQuery(id+"F1.opExtrude","CAP_EDGE",EDGE,{"disambiguationData":[OSD([subQ0])],"isStart":false})])]});}
            var Q4;
            {var subQ0=sQuery(id+"F0.wireOp",EDGE,"E9.45");Q4=makeQuery(id+"F29.opExtrude","SWEPT_FACE",FACE,{"disambiguationData":[OSD([subQ0]),TDD([makeQuery(id+"F1.opExtrude","CAP_EDGE",EDGE,{"disambiguationData":[OSD([subQ0])],"isStart":false})])]});}
            chamfer(context, id + "F39", {"entities" : qUnion([Q0, Q1, Q2, Q3, Q4]), "width" : 5.08 * mm, "tangentPropagation" : true});
        }
        {
            var Q0;
            {var subQ0=sQuery(id+"F0.wireOp",EDGE,"E9.33");Q0=makeQuery(id+"F11.boolean.opBoolean","MERGE",FACE,{"derivedFrom":[makeQuery(id+"F1.opExtrude","SWEPT_FACE",FACE,{"disambiguationData":[OSD([subQ0])]}),makeQuery(id+"F11.opExtrude","SWEPT_FACE",FACE,{"disambiguationData":[OSD([subQ0])]})]});}
            var sketch = newSketch(context, id + "F40", { "sketchPlane" : qUnion([Q0])});
            skLineSegment(sketch, "E33.bottom", {"start": v(25.4, 6.8) * mm, "end": v(-27.89, 6.8) * mm});
            skLineSegment(sketch, "E33.top", {"start": v(25.4, -6.8) * mm, "end": v(-27.89, -6.8) * mm});
            skLineSegment(sketch, "E33.left", {"start": v(25.4, 6.8) * mm, "end": v(25.4, -6.8) * mm});
            skLineSegment(sketch, "E33.right", {"start": v(-27.89, 6.8) * mm, "end": v(-27.89, -6.8) * mm});
            skSolve(sketch);
        }
        {
            var Q0;
            Q0=makeQuery(id+"F40.imprint","IMPRINT",FACE,{"disambiguationData":[TD([[makeQuery(id+"F40.imprint","IMPRINT",EDGE,{"derivedFrom":sQuery(id+"F40.wireOp",EDGE,"E33.bottom")}),1.0]])]});
            extrude(context, id + "F41", {"entities" : qUnion([Q0]), "oppositeDirection" : true, "depth" : 25.4 * mm});
        }
        {
            var Q0;
            Q0=makeQuery(id+"F41.opExtrude","SWEPT_FACE",FACE,{"disambiguationData":[OSD([sQuery(id+"F40.wireOp",EDGE,"E33.left")])]});
            chamfer(context, id + "F42", {"entities" : qUnion([Q0]), "width" : 5.08 * mm, "tangentPropagation" : true});
        }
        {
            var Q0;
            Q0=makeQuery(id+"F41.opExtrude","SWEPT_FACE",FACE,{"disambiguationData":[OSD([sQuery(id+"F40.wireOp",EDGE,"E33.right")])]});
            chamfer(context, id + "F43", {"entities" : qUnion([Q0]), "width" : 5.08 * mm, "tangentPropagation" : true});
        }
        {
            var Q0;
            {var subQ0=sQuery(id+"F0.wireOp",EDGE,"E9.16");Q0=makeQuery(id+"F11.boolean.opBoolean","MERGE",FACE,{"derivedFrom":[makeQuery(id+"F1.opExtrude","SWEPT_FACE",FACE,{"disambiguationData":[OSD([subQ0])]}),makeQuery(id+"F11.opExtrude","SWEPT_FACE",FACE,{"disambiguationData":[OSD([subQ0])]})]});}
            var sketch = newSketch(context, id + "F44", { "sketchPlane" : qUnion([Q0])});
            skLineSegment(sketch, "E34.bottom", {"start": v(-25.4, -6.8) * mm, "end": v(27.66, -6.8) * mm});
            skLineSegment(sketch, "E34.top", {"start": v(-25.4, 6.8) * mm, "end": v(27.66, 6.8) * mm});
            skLineSegment(sketch, "E34.left", {"start": v(-25.4, -6.8) * mm, "end": v(-25.4, 6.8) * mm});
            skLineSegment(sketch, "E34.right", {"start": v(27.66, -6.8) * mm, "end": v(27.66, 6.8) * mm});
            skSolve(sketch);
        }
        {
            var Q0;
            Q0=makeQuery(id+"F44.imprint","IMPRINT",FACE,{"disambiguationData":[TD([[makeQuery(id+"F44.imprint","IMPRINT",EDGE,{"derivedFrom":sQuery(id+"F44.wireOp",EDGE,"E34.bottom")}),1.0]])]});
            extrude(context, id + "F45", {"entities" : qUnion([Q0]), "oppositeDirection" : true, "depth" : 25.4 * mm});
        }
        {
            var Q0;
            {var subQ0=sQuery(id+"F0.wireOp",EDGE,"E9.49");Q0=makeQuery(id+"F11.boolean.opBoolean","MERGE",FACE,{"derivedFrom":[makeQuery(id+"F1.opExtrude","SWEPT_FACE",FACE,{"disambiguationData":[OSD([subQ0])]}),makeQuery(id+"F11.opExtrude","SWEPT_FACE",FACE,{"disambiguationData":[OSD([subQ0])]})]});}
            var sketch = newSketch(context, id + "F46", { "sketchPlane" : qUnion([Q0])});
            skLineSegment(sketch, "E35.bottom", {"start": v(1.66, 27.68) * mm, "end": v(-14.29, 27.68) * mm});
            skLineSegment(sketch, "E35.top", {"start": v(1.66, -25.3) * mm, "end": v(-14.29, -25.3) * mm});
            skLineSegment(sketch, "E35.left", {"start": v(1.66, 27.68) * mm, "end": v(1.66, -25.3) * mm});
            skLineSegment(sketch, "E35.right", {"start": v(-14.29, 27.68) * mm, "end": v(-14.29, -25.3) * mm});
            skSolve(sketch);
        }
        {
            var Q0;
            Q0=qSketchRegion(id+"F46",true);
            extrude(context, id + "F47", {"entities" : qUnion([Q0]), "oppositeDirection" : true, "depth" : 25.4 * mm});
        }
        {
            var Q0;
            Q0=makeQuery(id+"F47.opExtrude","SWEPT_FACE",FACE,{"disambiguationData":[OSD([sQuery(id+"F46.wireOp",EDGE,"E35.top")])]});
            var Q1;
            Q1=makeQuery(id+"F47.opExtrude","SWEPT_FACE",FACE,{"disambiguationData":[OSD([sQuery(id+"F46.wireOp",EDGE,"E35.bottom")])]});
            var Q2;
            Q2=makeQuery(id+"F45.opExtrude","SWEPT_FACE",FACE,{"disambiguationData":[OSD([sQuery(id+"F44.wireOp",EDGE,"E34.left")])]});
            var Q3;
            Q3=makeQuery(id+"F45.opExtrude","SWEPT_FACE",FACE,{"disambiguationData":[OSD([sQuery(id+"F44.wireOp",EDGE,"E34.right")])]});
            chamfer(context, id + "F48", {"entities" : qUnion([Q0, Q1, Q2, Q3]), "width" : 5.08 * mm, "tangentPropagation" : true});
        }
        {
            var Q0;
            Q0=makeQuery(id+"F2.opExtrude","CAP_FACE",FACE,{"disambiguationData":[OSD([sQuery(id+"F0.wireOp",EDGE,"E0.2"),sQuery(id+"F0.wireOp",EDGE,"E1.0"),sQuery(id+"F0.wireOp",EDGE,"E5"),sQuery(id+"F0.wireOp",EDGE,"E7")])],"isStart":false});
            var sketch = newSketch(context, id + "F49", { "sketchPlane" : qUnion([Q0])});
            skLineSegment(sketch, "E36", {"start": v(69.66, 49.5) * mm, "end": v(-70.53, 49.5) * mm});
            skLineSegment(sketch, "E37", {"start": v(-70.53, 49.5) * mm, "end": v(-79.18, 49.48) * mm});
            skLineSegment(sketch, "E38", {"start": v(69.66, 49.5) * mm, "end": v(78.32, 49.5) * mm});
            skLineSegment(sketch, "E39", {"start": v(-70.53, 49.5) * mm, "end": v(-21.26, 21.62) * mm});
            skLineSegment(sketch, "E40", {"start": v(-70.53, 49.5) * mm, "end": v(-70.54, 52.45) * mm});
            skLineSegment(sketch, "E41", {"start": v(69.66, 49.5) * mm, "end": v(21.37, 22.18) * mm});
            skLineSegment(sketch, "E42", {"start": v(69.66, 49.5) * mm, "end": v(69.66, 52.84) * mm});
            skLineSegment(sketch, "E43", {"start": v(21.37, 22.18) * mm, "end": v(-21.26, 21.62) * mm});
            skSolve(sketch);
        }
        {
            var Q0;
            Q0=makeQuery(id+"F49.imprint","IMPRINT",FACE,{"disambiguationData":[TD([[makeQuery(id+"F49.imprint","IMPRINT",EDGE,{"derivedFrom":sQuery(id+"F49.wireOp",EDGE,"E36")}),1.0]])]});
            extrude(context, id + "F50", {"entities" : qUnion([Q0]), "operationType" : NewBodyOperationType.REMOVE, "oppositeDirection" : true, "depth" : 1.27 * mm});
        }
        {
            var Q0;
            Q0=makeQuery(id+"F49.imprint","IMPRINT",FACE,{"disambiguationData":[TD([[makeQuery(id+"F49.imprint","IMPRINT",EDGE,{"derivedFrom":sQuery(id+"F49.wireOp",EDGE,"E36")}),1.0]])]});
            var sketch = newSketch(context, id + "F51", { "sketchPlane" : qUnion([Q0])});
            skLineSegment(sketch, "E44", {"start": v(8.1, -32.07) * mm, "end": v(30.75, 8.62) * mm});
            skLineSegment(sketch, "E45", {"start": v(30.75, 8.62) * mm, "end": v(79.3, 38.22) * mm});
            skLineSegment(sketch, "E46", {"start": v(79.3, 38.22) * mm, "end": v(8.1, -89.41) * mm});
            skLineSegment(sketch, "E47", {"start": v(8.1, -89.41) * mm, "end": v(8.1, -32.07) * mm});
            skSolve(sketch);
        }
        {
            var Q0;
            Q0=makeQuery(id+"F51.imprint","IMPRINT",FACE,{"disambiguationData":[TD([[makeQuery(id+"F51.imprint","IMPRINT",EDGE,{"derivedFrom":sQuery(id+"F51.wireOp",EDGE,"E44")}),-1.0]])]});
            extrude(context, id + "F52", {"entities" : qUnion([Q0]), "operationType" : NewBodyOperationType.REMOVE, "oppositeDirection" : true, "depth" : 1.27 * mm});
        }
        {
            var Q0;
            Q0=makeQuery(id+"F2.opExtrude","CAP_FACE",FACE,{"disambiguationData":[OSD([sQuery(id+"F0.wireOp",EDGE,"E0.1"),sQuery(id+"F0.wireOp",EDGE,"E1.2"),sQuery(id+"F0.wireOp",EDGE,"E3"),sQuery(id+"F0.wireOp",EDGE,"E4"),sQuery(id+"F0.wireOp",EDGE,"E6")])],"isStart":false});
            var sketch = newSketch(context, id + "F53", { "sketchPlane" : qUnion([Q0])});
            skLineSegment(sketch, "E48", {"start": v(-6.9, -89.21) * mm, "end": v(-7.45, -31.91) * mm});
            skLineSegment(sketch, "E49", {"start": v(-6.9, -89.21) * mm, "end": v(-80.78, 37.92) * mm});
            skLineSegment(sketch, "E50", {"start": v(-31.44, 8.72) * mm, "end": v(-80.78, 37.92) * mm});
            skLineSegment(sketch, "E51", {"start": v(-7.45, -31.91) * mm, "end": v(-31.44, 8.72) * mm});
            skSolve(sketch);
        }
        {
            var Q0;
            Q0=makeQuery(id+"F53.imprint","IMPRINT",FACE,{"disambiguationData":[TD([[makeQuery(id+"F53.imprint","IMPRINT",EDGE,{"derivedFrom":sQuery(id+"F53.wireOp",EDGE,"E48")}),1.0]])]});
            extrude(context, id + "F54", {"entities" : qUnion([Q0]), "operationType" : NewBodyOperationType.REMOVE, "oppositeDirection" : true, "depth" : 1.27 * mm});
        }
        {
            var Q0;
            {var subQ0=sQuery(id+"F0.wireOp",EDGE,"E9.21");Q0=makeQuery(id+"F31.opExtrude","SWEPT_FACE",FACE,{"disambiguationData":[OSD([subQ0]),TDD([makeQuery(id+"F11.opExtrude","CAP_EDGE",EDGE,{"disambiguationData":[OSD([subQ0])],"isStart":false})])]});}
            var Q1;
            {var subQ0=sQuery(id+"F0.wireOp",EDGE,"E9.11");Q1=makeQuery(id+"F26.opExtrude","SWEPT_FACE",FACE,{"disambiguationData":[OSD([subQ0]),TDD([makeQuery(id+"F11.opExtrude","CAP_EDGE",EDGE,{"disambiguationData":[OSD([subQ0])],"isStart":false})])]});}
            var Q2;
            {var subQ0=sQuery(id+"F0.wireOp",EDGE,"E9.28");Q2=makeQuery(id+"F30.opExtrude","SWEPT_FACE",FACE,{"disambiguationData":[OSD([subQ0]),TDD([makeQuery(id+"F11.opExtrude","CAP_EDGE",EDGE,{"disambiguationData":[OSD([subQ0])],"isStart":false})])]});}
            var Q3;
            {var subQ0=sQuery(id+"F0.wireOp",EDGE,"E9.38");Q3=makeQuery(id+"F28.opExtrude","SWEPT_FACE",FACE,{"disambiguationData":[OSD([subQ0]),TDD([makeQuery(id+"F11.opExtrude","CAP_EDGE",EDGE,{"disambiguationData":[OSD([subQ0])],"isStart":false})])]});}
            var Q4;
            {var subQ0=sQuery(id+"F0.wireOp",EDGE,"E9.45");Q4=makeQuery(id+"F29.opExtrude","SWEPT_FACE",FACE,{"disambiguationData":[OSD([subQ0]),TDD([makeQuery(id+"F11.opExtrude","CAP_EDGE",EDGE,{"disambiguationData":[OSD([subQ0])],"isStart":false})])]});}
            var Q5;
            {var subQ0=sQuery(id+"F0.wireOp",EDGE,"E9.4");Q5=makeQuery(id+"F27.opExtrude","SWEPT_FACE",FACE,{"disambiguationData":[OSD([subQ0]),TDD([makeQuery(id+"F11.opExtrude","CAP_EDGE",EDGE,{"disambiguationData":[OSD([subQ0])],"isStart":false})])]});}
            chamfer(context, id + "F55", {"entities" : qUnion([Q0, Q1, Q2, Q3, Q4, Q5]), "width" : 5.08 * mm, "tangentPropagation" : true});
        }
        {
            var Q0;
            Q0=makeQuery(id+"F1.opExtrude","SWEPT_FACE",FACE,{"disambiguationData":[OSD([sQuery(id+"F0.wireOp",EDGE,"E29.0")])]});
            chamfer(context, id + "F56", {"entities" : qUnion([Q0]), "width" : 5.08 * mm, "tangentPropagation" : true});
        }
        {
            var Q0;
            Q0=makeQuery(id+"F23.opLoft","SWEPT_FACE",FACE,{"disambiguationData":[OSD([sQuery(id+"F20.wireOp",EDGE,"E31"),sQuery(id+"F22.wireOp",EDGE,"E32")])]});
            var Q1;
            Q1=makeQuery(id+"F19.opChamfer","BLEND_FACE",FACE,{"disambiguationData":[OSD([sQuery(id+"F12.wireOp",EDGE,"E30")])]});
            var Q2;
            Q2=makeQuery(id+"F18.opExtrude","CAP_FACE",FACE,{"disambiguationData":[OSD([sQuery(id+"F12.wireOp",EDGE,"E30")])],"isStart":false});
            chamfer(context, id + "F57", {"entities" : qUnion([Q0, Q1, Q2]), "width" : 5.08 * mm, "tangentPropagation" : true});
        }
        {
            var Q0;
            {var subQ0=sQuery(id+"F12.wireOp",EDGE,"E30");Q0=makeQuery(id+"F17.opChamfer","BLEND_EDGE",EDGE,{"blendedFrom":[makeQuery(id+"F16.opExtrude","CAP_EDGE",EDGE,{"disambiguationData":[OSD([subQ0])],"isStart":false}),makeQuery(id+"F16.boolean.opBoolean","MERGE",FACE,{"derivedFrom":[makeQuery(id+"F15.boolean.opBoolean","MERGE",FACE,{"derivedFrom":[makeQuery(id+"F13.opExtrude","SWEPT_FACE",FACE,{"disambiguationData":[OSD([subQ0])]}),makeQuery(id+"F15.opExtrude","SWEPT_FACE",FACE,{"disambiguationData":[OSD([subQ0])]})]}),makeQuery(id+"F16.opExtrude","SWEPT_FACE",FACE,{"disambiguationData":[OSD([subQ0])]})]})],"blendedInto":[makeQuery(id+"F16.boolean.opBoolean","MERGE",FACE,{"derivedFrom":[makeQuery(id+"F15.boolean.opBoolean","MERGE",FACE,{"derivedFrom":[makeQuery(id+"F13.opExtrude","SWEPT_FACE",FACE,{"disambiguationData":[OSD([subQ0])]}),makeQuery(id+"F15.opExtrude","SWEPT_FACE",FACE,{"disambiguationData":[OSD([subQ0])]})]}),makeQuery(id+"F16.opExtrude","SWEPT_FACE",FACE,{"disambiguationData":[OSD([subQ0])]})]})]});}
            chamfer(context, id + "F58", {"entities" : qUnion([Q0]), "width" : 5.08 * mm, "tangentPropagation" : true});
        }
        {
            var Q0;
            Q0=makeQuery(id+"F4.opExtrude","CAP_FACE",FACE,{"disambiguationData":[OSD([sQuery(id+"F0.wireOp",EDGE,"E10.0"),sQuery(id+"F0.wireOp",EDGE,"E10.1"),sQuery(id+"F0.wireOp",EDGE,"E10.2")])],"isStart":false});
            cPlane(context, id + "F59", {"entities" : qUnion([Q0]), "cplaneType" : CPlaneType.OFFSET, "offset" : 6.35 * mm, "width" : 152.4 * mm, "height" : 152.4 * mm});
        }
        {
            var Q0;
            Q0=makeQuery(id+"F15.opExtrude","CAP_FACE",FACE,{"disambiguationData":[OSD([sQuery(id+"F12.wireOp",EDGE,"E30")])],"isStart":false});
            var sketch = newSketch(context, id + "F60", { "sketchPlane" : qUnion([Q0])});
            skCircle(sketch, "E52.cCircle", {"center": v(0, 0) * mm, "radius": 108.15 * mm, "construction": true});
            skLineSegment(sketch, "E52.0", {"start": v(-84.09, 68) * mm, "end": v(-68.11, 84) * mm});
            skLineSegment(sketch, "E52.1", {"start": v(-68.11, 84) * mm, "end": v(-49.16, 96.33) * mm});
            skLineSegment(sketch, "E52.2", {"start": v(-49.16, 96.33) * mm, "end": v(-28.05, 104.44) * mm});
            skLineSegment(sketch, "E52.3", {"start": v(-28.05, 104.44) * mm, "end": v(-5.73, 108) * mm});
            skLineSegment(sketch, "E52.4", {"start": v(-5.73, 108) * mm, "end": v(16.85, 106.83) * mm});
            skLineSegment(sketch, "E52.5", {"start": v(16.85, 106.83) * mm, "end": v(38.7, 100.99) * mm});
            skLineSegment(sketch, "E52.6", {"start": v(38.7, 100.99) * mm, "end": v(58.84, 90.74) * mm});
            skLineSegment(sketch, "E52.7", {"start": v(58.84, 90.74) * mm, "end": v(76.42, 76.52) * mm});
            skLineSegment(sketch, "E52.8", {"start": v(76.42, 76.52) * mm, "end": v(90.66, 58.96) * mm});
            skLineSegment(sketch, "E52.9", {"start": v(90.66, 58.96) * mm, "end": v(100.94, 38.82) * mm});
            skLineSegment(sketch, "E52.10", {"start": v(100.94, 38.82) * mm, "end": v(106.8, 16.98) * mm});
            skLineSegment(sketch, "E52.11", {"start": v(106.8, 16.98) * mm, "end": v(108, -5.6) * mm});
            skLineSegment(sketch, "E52.12", {"start": v(108, -5.6) * mm, "end": v(104.48, -27.93) * mm});
            skLineSegment(sketch, "E52.13", {"start": v(104.48, -27.93) * mm, "end": v(96.39, -49.04) * mm});
            skLineSegment(sketch, "E52.14", {"start": v(96.39, -49.04) * mm, "end": v(84.09, -68) * mm});
            skLineSegment(sketch, "E52.15", {"start": v(84.09, -68) * mm, "end": v(68.11, -84) * mm});
            skLineSegment(sketch, "E52.16", {"start": v(68.11, -84) * mm, "end": v(49.16, -96.33) * mm});
            skLineSegment(sketch, "E52.17", {"start": v(49.16, -96.33) * mm, "end": v(28.05, -104.44) * mm});
            skLineSegment(sketch, "E52.18", {"start": v(28.05, -104.44) * mm, "end": v(5.73, -108) * mm});
            skLineSegment(sketch, "E52.19", {"start": v(5.73, -108) * mm, "end": v(-16.85, -106.83) * mm});
            skLineSegment(sketch, "E52.20", {"start": v(-16.85, -106.83) * mm, "end": v(-38.7, -100.99) * mm});
            skLineSegment(sketch, "E52.21", {"start": v(-38.7, -100.99) * mm, "end": v(-58.84, -90.74) * mm});
            skLineSegment(sketch, "E52.22", {"start": v(-58.84, -90.74) * mm, "end": v(-76.42, -76.52) * mm});
            skLineSegment(sketch, "E52.23", {"start": v(-76.42, -76.52) * mm, "end": v(-90.66, -58.96) * mm});
            skLineSegment(sketch, "E52.24", {"start": v(-90.66, -58.96) * mm, "end": v(-100.94, -38.82) * mm});
            skLineSegment(sketch, "E52.25", {"start": v(-100.94, -38.82) * mm, "end": v(-106.8, -16.98) * mm});
            skLineSegment(sketch, "E52.26", {"start": v(-106.8, -16.98) * mm, "end": v(-108, 5.6) * mm});
            skLineSegment(sketch, "E52.27", {"start": v(-108, 5.6) * mm, "end": v(-104.48, 27.93) * mm});
            skLineSegment(sketch, "E52.28", {"start": v(-104.48, 27.93) * mm, "end": v(-96.39, 49.04) * mm});
            skLineSegment(sketch, "E52.29", {"start": v(-96.39, 49.04) * mm, "end": v(-84.09, 68) * mm});
            skSolve(sketch);
        }
        {
            var Q0;
            Q0 = qSketchRegion(id + "F60", true);
            extrude(context, id + "F61", {"entities" : qUnion([Q0]), "operationType" : NewBodyOperationType.ADD, "depth" : 50.8 * mm});
        }
        {
            var Q0;
            Q0=makeQuery(id+"F61.opExtrude","CAP_FACE",FACE,{"disambiguationData":[OSD([sQuery(id+"F60.wireOp",EDGE,"E52.0"),sQuery(id+"F60.wireOp",EDGE,"E52.1"),sQuery(id+"F60.wireOp",EDGE,"E52.2"),sQuery(id+"F60.wireOp",EDGE,"E52.3"),sQuery(id+"F60.wireOp",EDGE,"E52.4"),sQuery(id+"F60.wireOp",EDGE,"E52.5"),sQuery(id+"F60.wireOp",EDGE,"E52.6"),sQuery(id+"F60.wireOp",EDGE,"E52.7"),sQuery(id+"F60.wireOp",EDGE,"E52.8"),sQuery(id+"F60.wireOp",EDGE,"E52.9"),sQuery(id+"F60.wireOp",EDGE,"E52.10"),sQuery(id+"F60.wireOp",EDGE,"E52.11"),sQuery(id+"F60.wireOp",EDGE,"E52.12"),sQuery(id+"F60.wireOp",EDGE,"E52.13"),sQuery(id+"F60.wireOp",EDGE,"E52.14"),sQuery(id+"F60.wireOp",EDGE,"E52.15"),sQuery(id+"F60.wireOp",EDGE,"E52.16"),sQuery(id+"F60.wireOp",EDGE,"E52.17"),sQuery(id+"F60.wireOp",EDGE,"E52.18"),sQuery(id+"F60.wireOp",EDGE,"E52.19"),sQuery(id+"F60.wireOp",EDGE,"E52.20"),sQuery(id+"F60.wireOp",EDGE,"E52.21"),sQuery(id+"F60.wireOp",EDGE,"E52.22"),sQuery(id+"F60.wireOp",EDGE,"E52.23"),sQuery(id+"F60.wireOp",EDGE,"E52.24"),sQuery(id+"F60.wireOp",EDGE,"E52.25"),sQuery(id+"F60.wireOp",EDGE,"E52.26"),sQuery(id+"F60.wireOp",EDGE,"E52.27"),sQuery(id+"F60.wireOp",EDGE,"E52.28"),sQuery(id+"F60.wireOp",EDGE,"E52.29")])],"isStart":false});
            extrude(context, id + "F62", {"entities" : qUnion([Q0]), "operationType" : NewBodyOperationType.ADD, "oppositeDirection" : true, "depth" : 127 * mm});
        }
    });
